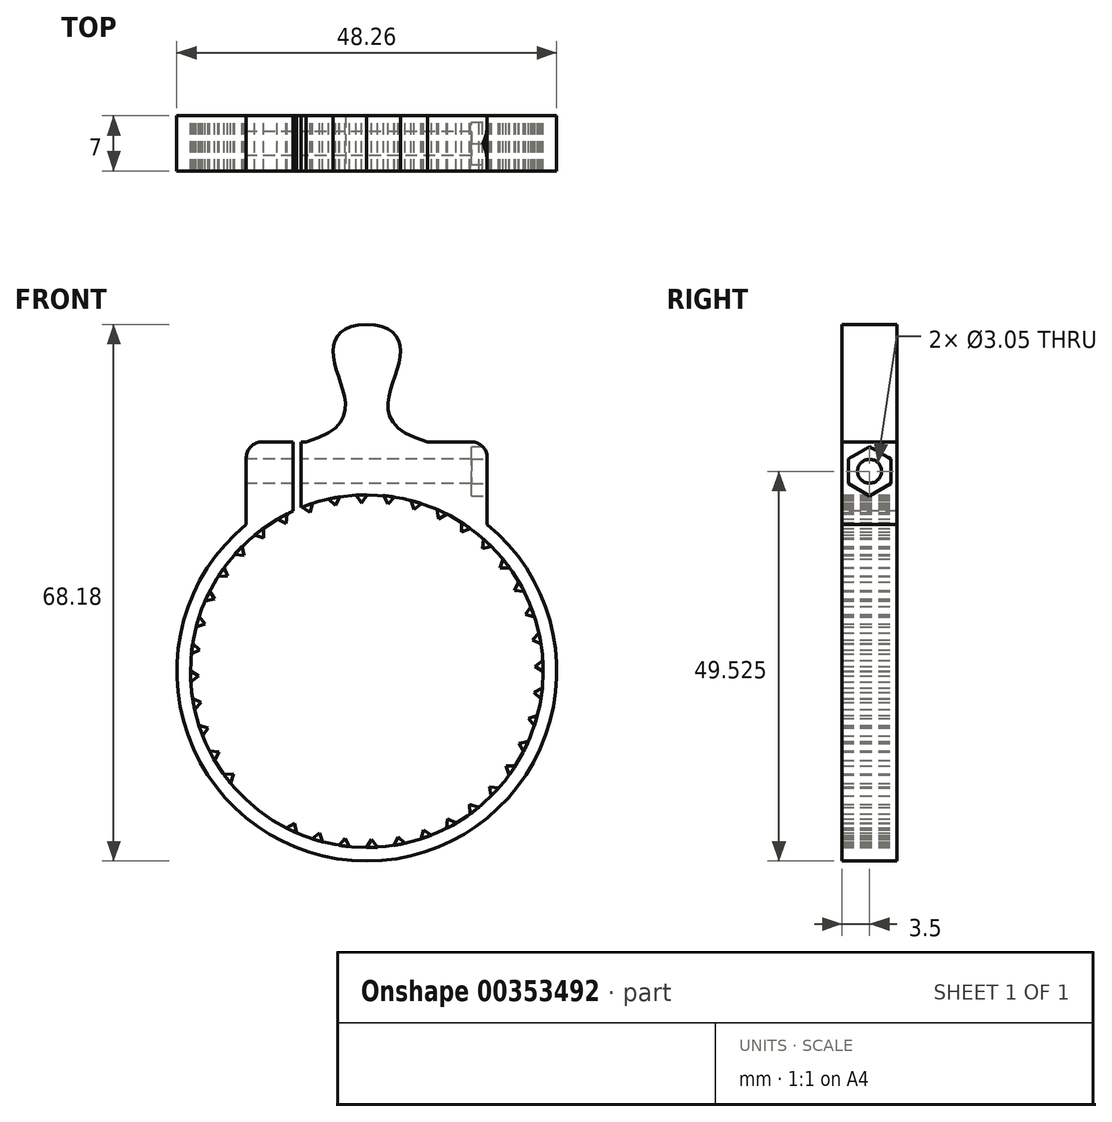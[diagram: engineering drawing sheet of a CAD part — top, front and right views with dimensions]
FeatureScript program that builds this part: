
annotation { "Feature Type Name" : "Feature", "Feature Type Description" : "" }
export const myFeature = defineFeature(function(context is Context, id is Id, definition is map)
    precondition{}
    {
        {
            var Q0;
            Q0=qCreatedBy(makeId("Front.planeOp"),FACE);
            var sketch = newSketch(context, id + "F0", { "sketchPlane" : qUnion([Q0])});
            skCircle(sketch, "E0", {"center": v(0, 0) * mm, "radius": 22.4 * mm});
            skCircle(sketch, "E1", {"center": v(0, 0) * mm, "radius": 24.12 * mm});
            skSolve(sketch);
        }
        {
            var Q0;
            Q0=qCreatedBy(makeId("Front.planeOp"),FACE);
            var sketch = newSketch(context, id + "F1", { "sketchPlane" : qUnion([Q0])});
            skLineSegment(sketch, "E2", {"start": v(8.94, 20.54) * mm, "end": v(9.15, 19.34) * mm});
            skLineSegment(sketch, "E3", {"start": v(9.15, 19.34) * mm, "end": v(10.2, 19.94) * mm});
            skArc(sketch, "E4", {"start": v(8.94, 20.54) * mm, "mid": v(9.58, 20.25) * mm, "end": v(10.2, 19.94) * mm});
            skSolve(sketch);
        }
        {
            var Q0;
            Q0=qCreatedBy(makeId("Front.planeOp"),FACE);
            var sketch = newSketch(context, id + "F2", { "sketchPlane" : qUnion([Q0])});
            skLineSegment(sketch, "E5", {"start": v(-15.3, 18.65) * mm, "end": v(-15.3, 27.12) * mm});
            skLineSegment(sketch, "E6", {"start": v(-13.3, 29.12) * mm, "end": v(0, 29.12) * mm});
            skPoint(sketch, "E7.visualSharp", {"position": v(-15.3, 29.12) * mm});
            skArc(sketch, "E7.filletArc", {"start": v(-13.3, 29.12) * mm, "mid": v(-14.71, 28.54) * mm, "end": v(-15.3, 27.12) * mm});
            skFitSpline(sketch, "E8", {"points": [v(-7.73, 29.12) * mm, v(-4.1, 39.1) * mm, v(0, 44.05) * mm], "startDerivative": vector(41.2, 11.2) * mm, "endDerivative": vector(26.64, 0.53) * mm});
            skFitSpline(sketch, "E9.MirrorCS", {"points": [v(7.73, 29.12) * mm, v(4.1, 39.1) * mm, v(0, 44.05) * mm], "startDerivative": vector(-41.2, 11.2) * mm, "endDerivative": vector(-26.64, 0.53) * mm});
            skLineSegment(sketch, "E10.MirrorCS", {"start": v(13.3, 29.12) * mm, "end": v(0, 29.12) * mm});
            skArc(sketch, "E11.MirrorCS", {"start": v(13.3, 29.12) * mm, "mid": v(14.71, 28.54) * mm, "end": v(15.3, 27.12) * mm});
            skLineSegment(sketch, "E12.MirrorCS", {"start": v(15.3, 18.65) * mm, "end": v(15.3, 27.12) * mm});
            skArc(sketch, "E13", {"start": v(-15.3, 18.65) * mm, "mid": v(0, 24.12) * mm, "end": v(15.3, 18.65) * mm});
            skPoint(sketch, "E14", {"position": v(-6.65, 29.12) * mm});
            skSolve(sketch);
        }
        {
            var Q0;
            Q0=makeQuery(id+"F0.imprint","IMPRINT",FACE,{"disambiguationData":[TD([[makeQuery(id+"F0.imprint","IMPRINT",EDGE,{"derivedFrom":sQuery(id+"F0.wireOp",EDGE,"E0")}),-1.0]])]});
            extrude(context, id + "F3", {"entities" : qUnion([Q0]), "depth" : 7 * mm});
        }
        {
            var Q0;
            Q0 = qSketchRegion(id + "F1", true);
            extrude(context, id + "F4", {"entities" : qUnion([Q0]), "depth" : 7 * mm});
        }
        {
            var Q0;
            Q0=makeQuery(id+"F4.opExtrude","SWEPT_BODY",BODY,{"disambiguationData":[OSD([sQuery(id+"F1.wireOp",EDGE,"E2"),sQuery(id+"F1.wireOp",EDGE,"E3"),sQuery(id+"F1.wireOp",EDGE,"E4")])]});
            var Q1;
            Q1=makeQuery(id+"F3.opExtrude","CAP_EDGE",EDGE,{"disambiguationData":[OSD([sQuery(id+"F0.wireOp",EDGE,"E0")])],"isStart":false});
            circularPattern(context, id + "F5", {"entities" : qUnion([Q0]), "axis" : qUnion([Q1]), "angle" : 360 * degree, "instanceCount" : 40, "equalSpace" : true});
        }
        {
            var Q0;
            Q0 = qSketchRegion(id + "F2", true);
            extrude(context, id + "F6", {"entities" : qUnion([Q0]), "operationType" : NewBodyOperationType.ADD, "depth" : 7 * mm});
        }
        {
            var Q0;
            Q0=makeQuery(id+"F6.opExtrude","SWEPT_FACE",FACE,{"disambiguationData":[OSD([sQuery(id+"F2.wireOp",EDGE,"E5")])]});
            var sketch = newSketch(context, id + "F7", { "sketchPlane" : qUnion([Q0])});
            skCircle(sketch, "E15", {"center": v(3.5, 25.4) * mm, "radius": 1.52 * mm});
            skLineSegment(sketch, "E16", {"start": v(3.5, 27.12) * mm, "end": v(3.5, 18.65) * mm, "construction": true});
            skSolve(sketch);
        }
        {
            var Q0;
            Q0=makeQuery(id+"F7.imprint","IMPRINT",FACE,{"disambiguationData":[TD([[makeQuery(id+"F7.imprint","IMPRINT",EDGE,{"derivedFrom":sQuery(id+"F7.wireOp",EDGE,"E15")}),1.0]])]});
            extrude(context, id + "F8", {"entities" : qUnion([Q0]), "operationType" : NewBodyOperationType.REMOVE, "endBound" : BoundingType.THROUGH_ALL, "oppositeDirection" : true, "depth" : 25 * mm});
        }
        {
            var Q0;
            Q0=makeQuery(id+"F6.boolean.opBoolean","MERGE",FACE,{"derivedFrom":[makeQuery(id+"F3.opExtrude","CAP_FACE",FACE,{"disambiguationData":[OSD([sQuery(id+"F0.wireOp",EDGE,"E0"),sQuery(id+"F0.wireOp",EDGE,"E1")])],"isStart":false}),makeQuery(id+"F6.opExtrude","CAP_FACE",FACE,{"disambiguationData":[OSD([sQuery(id+"F2.wireOp",EDGE,"E5"),sQuery(id+"F2.wireOp",EDGE,"E6"),sQuery(id+"F2.wireOp",EDGE,"E7.filletArc"),sQuery(id+"F2.wireOp",EDGE,"E8"),sQuery(id+"F2.wireOp",EDGE,"E9.MirrorCS"),sQuery(id+"F2.wireOp",EDGE,"E10.MirrorCS"),sQuery(id+"F2.wireOp",EDGE,"E11.MirrorCS"),sQuery(id+"F2.wireOp",EDGE,"E12.MirrorCS"),sQuery(id+"F2.wireOp",EDGE,"E13")])],"isStart":false})]});
            var sketch = newSketch(context, id + "F9", { "sketchPlane" : qUnion([Q0])});
            skLineSegment(sketch, "E17.bottom", {"start": v(-9.36, 29.12) * mm, "end": v(-8.36, 29.12) * mm});
            skLineSegment(sketch, "E17.top", {"start": v(-9.36, 20.35) * mm, "end": v(-8.36, 20.35) * mm});
            skLineSegment(sketch, "E17.left", {"start": v(-9.36, 29.12) * mm, "end": v(-9.36, 20.35) * mm});
            skLineSegment(sketch, "E17.right", {"start": v(-8.36, 29.12) * mm, "end": v(-8.36, 20.35) * mm});
            skSolve(sketch);
        }
        {
            var Q0;
            Q0 = qSketchRegion(id + "F9", true);
            extrude(context, id + "F10", {"entities" : qUnion([Q0]), "operationType" : NewBodyOperationType.REMOVE, "endBound" : BoundingType.THROUGH_ALL, "oppositeDirection" : true, "depth" : 25 * mm});
        }
        {
            var Q0;
            Q0=makeQuery(id+"F6.opExtrude","SWEPT_FACE",FACE,{"disambiguationData":[OSD([sQuery(id+"F2.wireOp",EDGE,"E12.MirrorCS")])]});
            var sketch = newSketch(context, id + "F11", { "sketchPlane" : qUnion([Q0])});
            skCircle(sketch, "E18.cCircle", {"center": v(-3.5, 25.4) * mm, "radius": 2.7 * mm, "construction": true});
            skLineSegment(sketch, "E18.0", {"start": v(-6.2, 23.84) * mm, "end": v(-6.2, 26.95) * mm});
            skLineSegment(sketch, "E18.1", {"start": v(-6.2, 26.95) * mm, "end": v(-3.5, 28.51) * mm});
            skLineSegment(sketch, "E18.2", {"start": v(-3.5, 28.51) * mm, "end": v(-0.8, 26.95) * mm});
            skLineSegment(sketch, "E18.3", {"start": v(-0.8, 26.95) * mm, "end": v(-0.8, 23.84) * mm});
            skLineSegment(sketch, "E18.4", {"start": v(-0.8, 23.84) * mm, "end": v(-3.5, 22.28) * mm});
            skLineSegment(sketch, "E18.5", {"start": v(-3.5, 22.28) * mm, "end": v(-6.2, 23.84) * mm});
            skPoint(sketch, "E18.0.midPoint", {"position": v(-6.2, 25.4) * mm});
            skPoint(sketch, "E19", {"position": v(-3.5, 27.12) * mm});
            skLineSegment(sketch, "E20", {"start": v(-3.5, 27.12) * mm, "end": v(-3.5, 46.05) * mm, "construction": true});
            skLineSegment(sketch, "E21", {"start": v(-3.5, 28.51) * mm, "end": v(-3.5, 3.94) * mm, "construction": true});
            skSolve(sketch);
        }
        {
            var Q0;
            {var subQ6=sQuery(id+"F11.wireOp",EDGE,"E18.0");Q0=makeQuery(id+"F11.imprint","IMPRINT",FACE,{"disambiguationData":[TD([[makeQuery(id+"F11.imprint","IMPRINT",EDGE,{"derivedFrom":subQ6}),-1.0]])]});}
            var Q1;
            {var subQ0=sQuery(id+"F11.wireOp",EDGE,"E18.2");var subQ1=sQuery(id+"F11.wireOp",EDGE,"E18.1");var subQ2=makeQuery(id+"F11.imprint","INTERSECT",VERTEX,{"derivedFrom":[subQ1,subQ0]});Q1=makeQuery(id+"F11.imprint","IMPRINT",FACE,{"disambiguationData":[TD([[makeQuery(id+"F11.imprint","IMPRINT",EDGE,{"disambiguationData":[TD([[subQ2,1.0]])],"derivedFrom":subQ1}),-1.0]])]});}
            extrude(context, id + "F12", {"entities" : qUnion([Q0, Q1]), "operationType" : NewBodyOperationType.REMOVE, "oppositeDirection" : true, "depth" : 2 * mm});
        }
        {
            var Q0;
            Q0=makeQuery(id+"F5.opPattern","COPY",BODY,{"derivedFrom":makeQuery(id+"F4.opExtrude","SWEPT_BODY",BODY,{"disambiguationData":[OSD([sQuery(id+"F1.wireOp",EDGE,"E2"),sQuery(id+"F1.wireOp",EDGE,"E3"),sQuery(id+"F1.wireOp",EDGE,"E4")])]}),"instanceName":"18"});
            var Q1;
            Q1=makeQuery(id+"F5.opPattern","COPY",BODY,{"derivedFrom":makeQuery(id+"F4.opExtrude","SWEPT_BODY",BODY,{"disambiguationData":[OSD([sQuery(id+"F1.wireOp",EDGE,"E2"),sQuery(id+"F1.wireOp",EDGE,"E3"),sQuery(id+"F1.wireOp",EDGE,"E4")])]}),"instanceName":"19"});
            deleteBodies(context, id + "F13", {"entities" : qUnion([Q0, Q1])});
        }
    });
